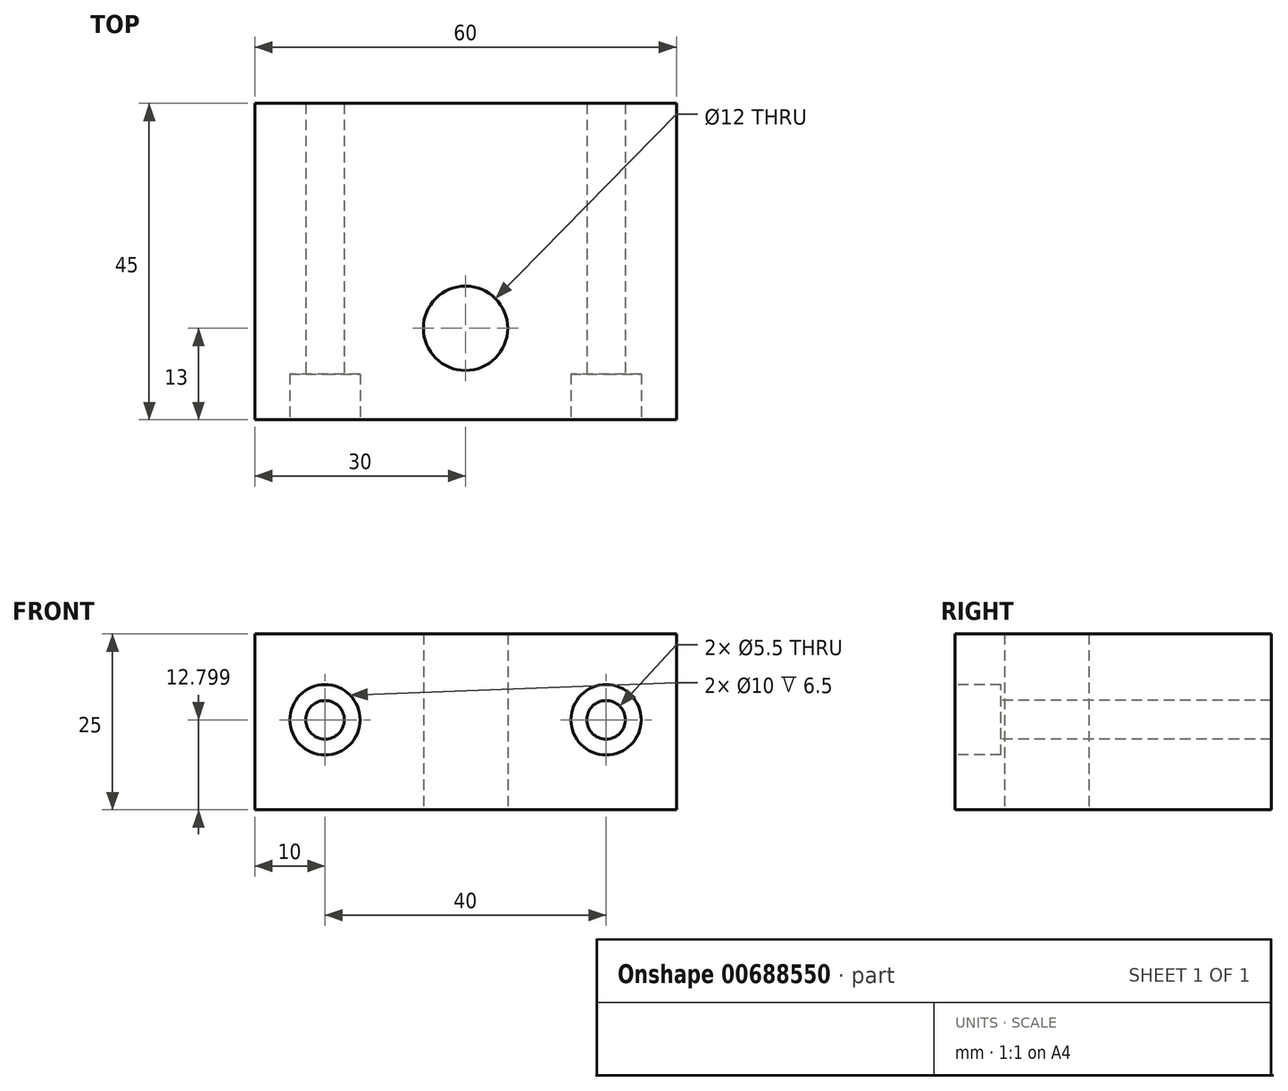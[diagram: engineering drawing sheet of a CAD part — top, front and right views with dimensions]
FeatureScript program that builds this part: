
annotation { "Feature Type Name" : "Feature", "Feature Type Description" : "" }
export const myFeature = defineFeature(function(context is Context, id is Id, definition is map)
    precondition{}
    {
        {
            var Q0;
            Q0=qCreatedBy(makeId("Top.planeOp"),FACE);
            var sketch = newSketch(context, id + "F0", { "sketchPlane" : qUnion([Q0])});
            skLineSegment(sketch, "E0.bottom", {"start": v(30, -22.5) * mm, "end": v(-30, -22.5) * mm});
            skLineSegment(sketch, "E0.top", {"start": v(30, 22.5) * mm, "end": v(-30, 22.5) * mm});
            skLineSegment(sketch, "E0.left", {"start": v(30, -22.5) * mm, "end": v(30, 22.5) * mm});
            skLineSegment(sketch, "E0.right", {"start": v(-30, -22.5) * mm, "end": v(-30, 22.5) * mm});
            skPoint(sketch, "E0.middle", {"position": v(0, 0) * mm});
            skCircle(sketch, "E1", {"center": v(0, -9.5) * mm, "radius": 6 * mm});
            skSolve(sketch);
        }
        {
            var Q0;
            Q0=makeQuery(id+"F0.imprint","IMPRINT",FACE,{"disambiguationData":[TD([[makeQuery(id+"F0.imprint","IMPRINT",EDGE,{"derivedFrom":sQuery(id+"F0.wireOp",EDGE,"E0.bottom")}),-1.0]])]});
            extrude(context, id + "F1", {"entities" : qUnion([Q0]), "depth" : 25 * mm, "offsetDistance" : 25 * mm});
        }
        {
            var Q0;
            Q0=makeQuery(id+"F1.opExtrude","SWEPT_FACE",FACE,{"disambiguationData":[OSD([sQuery(id+"F0.wireOp",EDGE,"E0.bottom")])]});
            var sketch = newSketch(context, id + "F2", { "sketchPlane" : qUnion([Q0])});
            skCircle(sketch, "E2", {"center": v(-20, 12.8) * mm, "radius": 2.75 * mm});
            skCircle(sketch, "E3", {"center": v(20, 12.8) * mm, "radius": 2.75 * mm});
            skCircle(sketch, "E4", {"center": v(-20, 12.8) * mm, "radius": 5 * mm});
            skCircle(sketch, "E5", {"center": v(20, 12.8) * mm, "radius": 5 * mm});
            skSolve(sketch);
        }
        {
            var Q0;
            Q0=makeQuery(id+"F2.imprint","IMPRINT",FACE,{"disambiguationData":[TD([[makeQuery(id+"F2.imprint","IMPRINT",EDGE,{"derivedFrom":sQuery(id+"F2.wireOp",EDGE,"E2")}),1.0]])]});
            var Q1;
            Q1=makeQuery(id+"F2.imprint","IMPRINT",FACE,{"disambiguationData":[TD([[makeQuery(id+"F2.imprint","IMPRINT",EDGE,{"derivedFrom":sQuery(id+"F2.wireOp",EDGE,"E3")}),1.0]])]});
            extrude(context, id + "F3", {"entities" : qUnion([Q0, Q1]), "operationType" : NewBodyOperationType.REMOVE, "oppositeDirection" : true, "depth" : 45 * mm, "offsetDistance" : 25 * mm});
        }
        {
            var Q0;
            Q0=makeQuery(id+"F2.imprint","IMPRINT",FACE,{"disambiguationData":[TD([[makeQuery(id+"F2.imprint","IMPRINT",EDGE,{"derivedFrom":sQuery(id+"F2.wireOp",EDGE,"E2")}),-1.0]])]});
            var Q1;
            Q1=makeQuery(id+"F2.imprint","IMPRINT",FACE,{"disambiguationData":[TD([[makeQuery(id+"F2.imprint","IMPRINT",EDGE,{"derivedFrom":sQuery(id+"F2.wireOp",EDGE,"E3")}),-1.0]])]});
            extrude(context, id + "F4", {"entities" : qUnion([Q0, Q1]), "operationType" : NewBodyOperationType.REMOVE, "oppositeDirection" : true, "depth" : 6.5 * mm, "offsetDistance" : 25 * mm});
        }
    });
